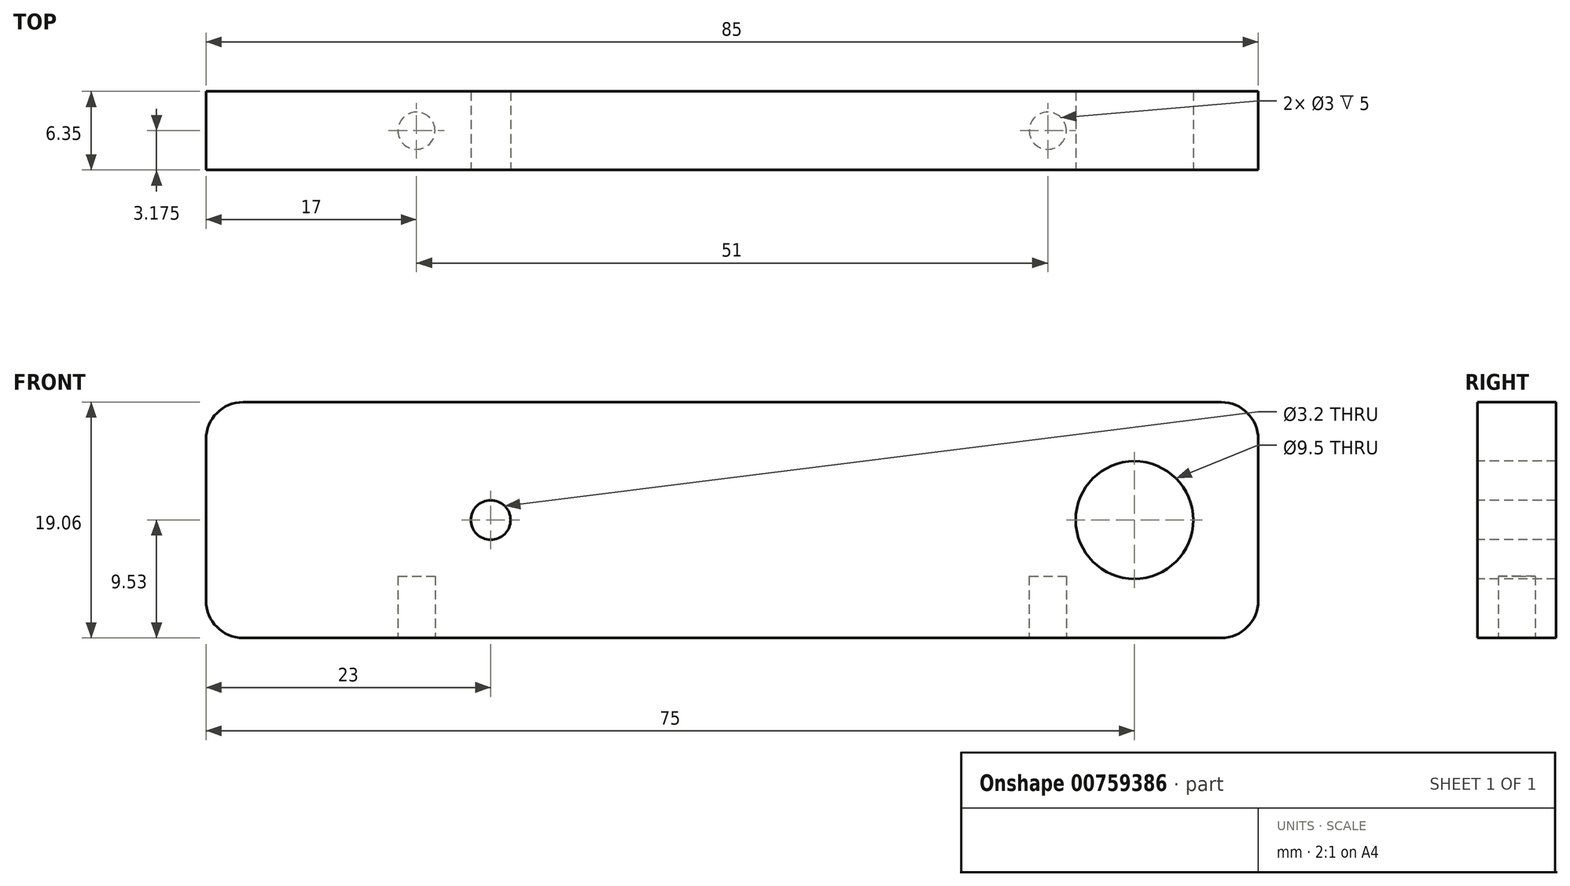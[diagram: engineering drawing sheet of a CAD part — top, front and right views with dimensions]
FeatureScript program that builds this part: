
annotation { "Feature Type Name" : "Feature", "Feature Type Description" : "" }
export const myFeature = defineFeature(function(context is Context, id is Id, definition is map)
    precondition{}
    {
        {
            var Q0;
            Q0=qCreatedBy(makeId("Front.planeOp"),FACE);
            var sketch = newSketch(context, id + "F0", { "sketchPlane" : qUnion([Q0])});
            skLineSegment(sketch, "E0.bottom", {"start": v(-39.5, 9.53) * mm, "end": v(39.5, 9.53) * mm});
            skLineSegment(sketch, "E0.top", {"start": v(-39.5, -9.53) * mm, "end": v(39.5, -9.53) * mm});
            skLineSegment(sketch, "E0.left", {"start": v(-42.5, 6.53) * mm, "end": v(-42.5, -6.53) * mm});
            skLineSegment(sketch, "E0.right", {"start": v(42.5, 6.52) * mm, "end": v(42.5, -6.53) * mm});
            skPoint(sketch, "E0.middle", {"position": v(0, 0) * mm});
            skPoint(sketch, "E1.visualSharp", {"position": v(-42.5, 9.53) * mm});
            skArc(sketch, "E1.filletArc", {"start": v(-39.5, 9.53) * mm, "mid": v(-41.62, 8.65) * mm, "end": v(-42.5, 6.53) * mm});
            skPoint(sketch, "E2.visualSharp", {"position": v(42.5, 9.53) * mm});
            skArc(sketch, "E2.filletArc", {"start": v(42.5, 6.52) * mm, "mid": v(41.62, 8.65) * mm, "end": v(39.5, 9.53) * mm});
            skPoint(sketch, "E3.visualSharp", {"position": v(42.5, -9.53) * mm});
            skArc(sketch, "E3.filletArc", {"start": v(39.5, -9.53) * mm, "mid": v(41.62, -8.65) * mm, "end": v(42.5, -6.53) * mm});
            skPoint(sketch, "E4.visualSharp", {"position": v(-42.5, -9.53) * mm});
            skArc(sketch, "E4.filletArc", {"start": v(-42.5, -6.53) * mm, "mid": v(-41.62, -8.65) * mm, "end": v(-39.5, -9.53) * mm});
            skCircle(sketch, "E5", {"center": v(-19.5, 0) * mm, "radius": 1.6 * mm});
            skCircle(sketch, "E6", {"center": v(32.5, 0) * mm, "radius": 4.75 * mm});
            skSolve(sketch);
        }
        {
            var Q0;
            Q0=makeQuery(id+"F0.imprint","IMPRINT",FACE,{"disambiguationData":[TD([[makeQuery(id+"F0.imprint","IMPRINT",EDGE,{"derivedFrom":sQuery(id+"F0.wireOp",EDGE,"E0.bottom")}),-1.0]])]});
            extrude(context, id + "F1", {"entities" : qUnion([Q0]), "oppositeDirection" : true, "depth" : 6.35 * mm, "offsetDistance" : 25 * mm});
        }
        {
            var Q0;
            Q0=makeQuery(id+"F1.opExtrude","SWEPT_FACE",FACE,{"disambiguationData":[OSD([sQuery(id+"F0.wireOp",EDGE,"E0.top")])]});
            var sketch = newSketch(context, id + "F2", { "sketchPlane" : qUnion([Q0])});
            skCircle(sketch, "E7", {"center": v(-25.5, -3.17) * mm, "radius": 1.5 * mm});
            skSolve(sketch);
        }
        {
            var Q0;
            Q0 = qSketchRegion(id + "F2", true);
            extrude(context, id + "F3", {"entities" : qUnion([Q0]), "operationType" : NewBodyOperationType.REMOVE, "oppositeDirection" : true, "depth" : 5 * mm, "offsetDistance" : 25 * mm});
        }
        {
            var Q0;
            Q0=makeQuery(id+"F1.opExtrude","SWEPT_FACE",FACE,{"disambiguationData":[OSD([sQuery(id+"F0.wireOp",EDGE,"E0.top")])]});
            var sketch = newSketch(context, id + "F4", { "sketchPlane" : qUnion([Q0])});
            skCircle(sketch, "E8", {"center": v(25.5, -3.17) * mm, "radius": 1.5 * mm});
            skSolve(sketch);
        }
        {
            var Q0;
            Q0 = qSketchRegion(id + "F4", true);
            extrude(context, id + "F5", {"entities" : qUnion([Q0]), "operationType" : NewBodyOperationType.REMOVE, "oppositeDirection" : true, "depth" : 5 * mm, "offsetDistance" : 25 * mm});
        }
    });
